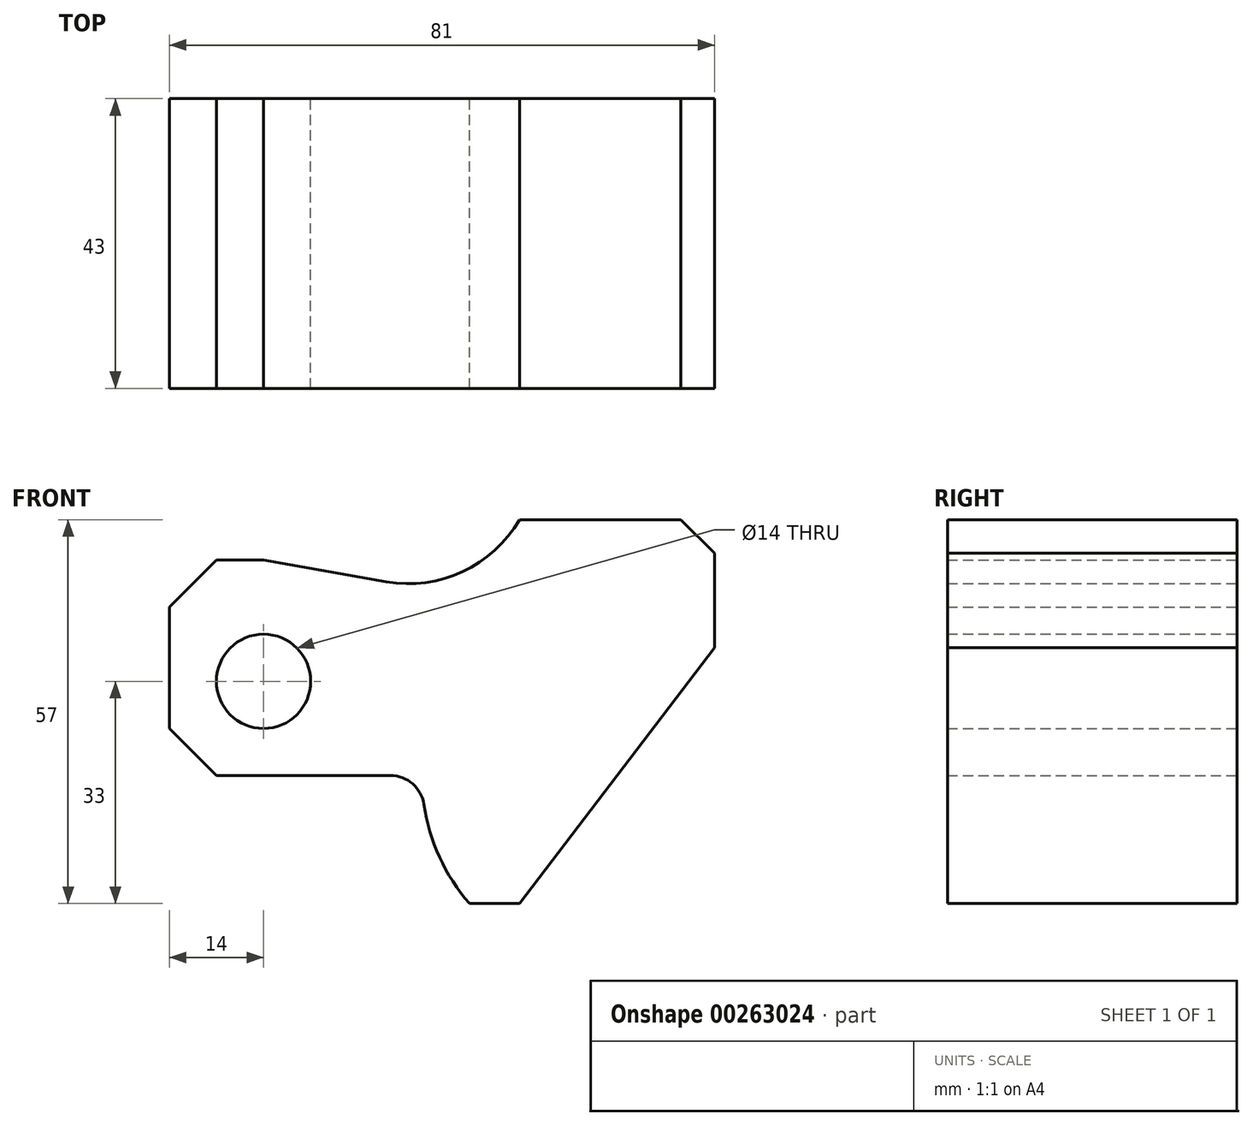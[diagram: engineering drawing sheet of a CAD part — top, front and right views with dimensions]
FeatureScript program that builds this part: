
annotation { "Feature Type Name" : "Feature", "Feature Type Description" : "" }
export const myFeature = defineFeature(function(context is Context, id is Id, definition is map)
    precondition{}
    {
        {
            var Q0;
            Q0=qCreatedBy(makeId("Front.planeOp"),FACE);
            var sketch = newSketch(context, id + "F0", { "sketchPlane" : qUnion([Q0])});
            skCircle(sketch, "E0", {"center": v(0, 0) * mm, "radius": 7 * mm});
            skLineSegment(sketch, "E1", {"start": v(0, 18) * mm, "end": v(-7, 18) * mm});
            skLineSegment(sketch, "E2", {"start": v(-7, 18) * mm, "end": v(-14, 11) * mm});
            skLineSegment(sketch, "E3", {"start": v(-14, 11) * mm, "end": v(-14, -7) * mm});
            skLineSegment(sketch, "E4", {"start": v(-14, -7) * mm, "end": v(-7, -14) * mm});
            skLineSegment(sketch, "E5", {"start": v(-7, -14) * mm, "end": v(18.87, -14) * mm});
            skArc(sketch, "E6", {"start": v(23.82, -18.26) * mm, "mid": v(22.13, -15.21) * mm, "end": v(18.87, -14) * mm});
            skArc(sketch, "E7", {"start": v(23.82, -18.26) * mm, "mid": v(26.15, -26.12) * mm, "end": v(30.6, -33) * mm});
            skLineSegment(sketch, "E8", {"start": v(30.6, -33) * mm, "end": v(38, -33) * mm});
            skLineSegment(sketch, "E9", {"start": v(38, -33) * mm, "end": v(67, 5) * mm});
            skLineSegment(sketch, "E10", {"start": v(67, 5) * mm, "end": v(67, 19) * mm});
            skLineSegment(sketch, "E11", {"start": v(67, 19) * mm, "end": v(62, 24) * mm});
            skLineSegment(sketch, "E12", {"start": v(62, 24) * mm, "end": v(38, 24) * mm});
            skArc(sketch, "E13", {"start": v(18.24, 14.78) * mm, "mid": v(29.57, 16.28) * mm, "end": v(38, 24) * mm});
            skLineSegment(sketch, "E14", {"start": v(0, 18) * mm, "end": v(18.24, 14.78) * mm});
            skLineSegment(sketch, "E15", {"start": v(0, 18) * mm, "end": v(21.55, 18) * mm, "construction": true});
            skSolve(sketch);
        }
        {
            var Q0;
            Q0=makeQuery(id+"F0.imprint","IMPRINT",FACE,{"disambiguationData":[TD([[makeQuery(id+"F0.imprint","IMPRINT",EDGE,{"derivedFrom":sQuery(id+"F0.wireOp",EDGE,"E0")}),-1.0]])]});
            extrude(context, id + "F1", {"entities" : qUnion([Q0]), "depth" : 43 * mm});
        }
    });
